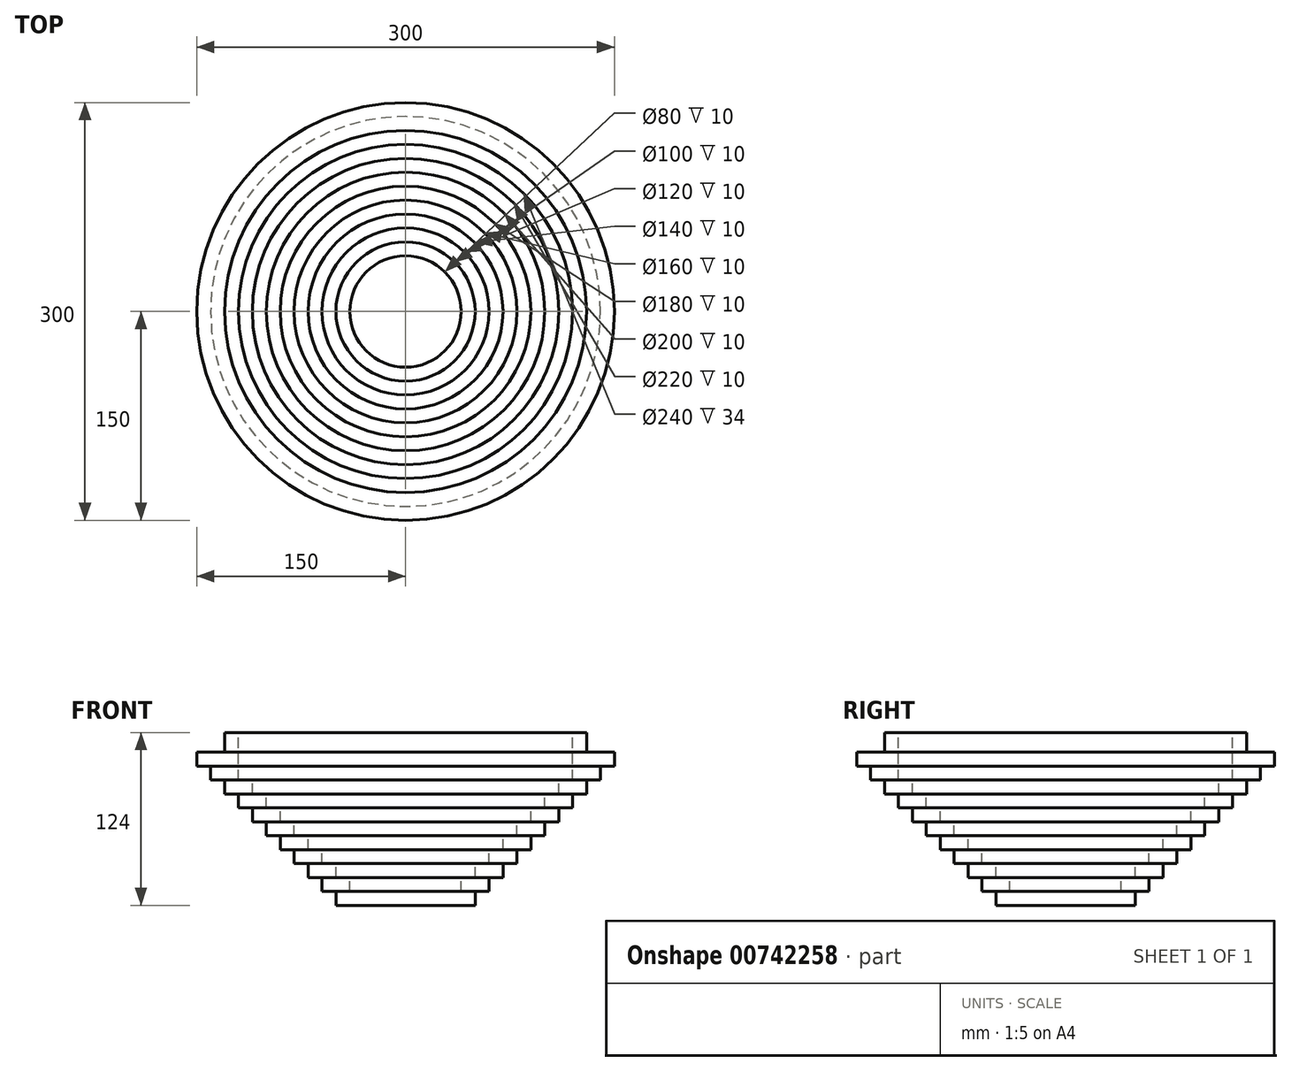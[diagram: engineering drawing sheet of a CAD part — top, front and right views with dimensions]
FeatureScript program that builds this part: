
annotation { "Feature Type Name" : "Feature", "Feature Type Description" : "" }
export const myFeature = defineFeature(function(context is Context, id is Id, definition is map)
    precondition{}
    {
        {
            var Q0;
            Q0=qCreatedBy(makeId("Front.planeOp"),FACE);
            var sketch = newSketch(context, id + "F0", { "sketchPlane" : qUnion([Q0])});
            skLineSegment(sketch, "E0", {"start": v(0, 0) * mm, "end": v(50, 0) * mm});
            skLineSegment(sketch, "E1", {"start": v(50, 0) * mm, "end": v(50, 10) * mm});
            skLineSegment(sketch, "E2", {"start": v(50, 10) * mm, "end": v(60, 10) * mm});
            skLineSegment(sketch, "E3", {"start": v(60, 10) * mm, "end": v(60, 20) * mm});
            skLineSegment(sketch, "E4", {"start": v(60, 20) * mm, "end": v(70, 20) * mm});
            skLineSegment(sketch, "E5", {"start": v(70, 20) * mm, "end": v(70, 30) * mm});
            skLineSegment(sketch, "E6", {"start": v(70, 30) * mm, "end": v(80, 30) * mm});
            skLineSegment(sketch, "E7", {"start": v(80, 30) * mm, "end": v(80, 40) * mm});
            skLineSegment(sketch, "E8", {"start": v(80, 40) * mm, "end": v(90, 40) * mm});
            skLineSegment(sketch, "E9", {"start": v(90, 40) * mm, "end": v(90, 50) * mm});
            skLineSegment(sketch, "E10", {"start": v(90, 50) * mm, "end": v(100, 50) * mm});
            skLineSegment(sketch, "E11", {"start": v(100, 50) * mm, "end": v(100, 60) * mm});
            skLineSegment(sketch, "E12", {"start": v(100, 60) * mm, "end": v(110, 60) * mm});
            skLineSegment(sketch, "E13", {"start": v(110, 60) * mm, "end": v(110, 70) * mm});
            skLineSegment(sketch, "E14", {"start": v(110, 70) * mm, "end": v(120, 70) * mm});
            skLineSegment(sketch, "E15", {"start": v(120, 70) * mm, "end": v(120, 80) * mm});
            skLineSegment(sketch, "E16", {"start": v(120, 80) * mm, "end": v(130, 80) * mm});
            skLineSegment(sketch, "E17", {"start": v(130, 80) * mm, "end": v(130, 90) * mm});
            skLineSegment(sketch, "E18", {"start": v(130, 90) * mm, "end": v(140, 90) * mm});
            skLineSegment(sketch, "E19", {"start": v(140, 90) * mm, "end": v(140, 100) * mm});
            skLineSegment(sketch, "E20", {"start": v(140, 100) * mm, "end": v(150, 100) * mm});
            skLineSegment(sketch, "E21", {"start": v(150, 100) * mm, "end": v(150, 110) * mm});
            skLineSegment(sketch, "E22.0", {"start": v(130, 100) * mm, "end": v(130, 110) * mm});
            skLineSegment(sketch, "E22.1", {"start": v(120, 100) * mm, "end": v(130, 100) * mm});
            skLineSegment(sketch, "E22.2", {"start": v(120, 90) * mm, "end": v(120, 100) * mm});
            skLineSegment(sketch, "E22.3", {"start": v(110, 90) * mm, "end": v(120, 90) * mm});
            skLineSegment(sketch, "E22.4", {"start": v(110, 80) * mm, "end": v(110, 90) * mm});
            skLineSegment(sketch, "E22.5", {"start": v(100, 80) * mm, "end": v(110, 80) * mm});
            skLineSegment(sketch, "E22.6", {"start": v(100, 70) * mm, "end": v(100, 80) * mm});
            skLineSegment(sketch, "E22.7", {"start": v(90, 70) * mm, "end": v(100, 70) * mm});
            skLineSegment(sketch, "E22.8", {"start": v(90, 60) * mm, "end": v(90, 70) * mm});
            skLineSegment(sketch, "E22.9", {"start": v(80, 60) * mm, "end": v(90, 60) * mm});
            skLineSegment(sketch, "E22.10", {"start": v(50, 20) * mm, "end": v(50, 30) * mm});
            skLineSegment(sketch, "E22.11", {"start": v(40, 20) * mm, "end": v(50, 20) * mm});
            skLineSegment(sketch, "E22.12", {"start": v(40, 10) * mm, "end": v(40, 20) * mm});
            skLineSegment(sketch, "E22.13", {"start": v(0, 10) * mm, "end": v(40, 10) * mm});
            skLineSegment(sketch, "E22.14", {"start": v(50, 30) * mm, "end": v(60, 30) * mm});
            skLineSegment(sketch, "E22.15", {"start": v(60, 30) * mm, "end": v(60, 40) * mm});
            skLineSegment(sketch, "E22.16", {"start": v(60, 40) * mm, "end": v(70, 40) * mm});
            skLineSegment(sketch, "E22.17", {"start": v(70, 40) * mm, "end": v(70, 50) * mm});
            skLineSegment(sketch, "E22.18", {"start": v(70, 50) * mm, "end": v(80, 50) * mm});
            skLineSegment(sketch, "E22.19", {"start": v(80, 50) * mm, "end": v(80, 60) * mm});
            skLineSegment(sketch, "E23", {"start": v(150, 110) * mm, "end": v(130, 110) * mm});
            skLineSegment(sketch, "E24", {"start": v(0, 10) * mm, "end": v(0, 0) * mm});
            skSolve(sketch);
        }
        {
            var Q0;
            Q0=makeQuery(id+"F0.imprint","IMPRINT",FACE,{"disambiguationData":[TD([[makeQuery(id+"F0.imprint","IMPRINT",EDGE,{"derivedFrom":sQuery(id+"F0.wireOp",EDGE,"E0")}),1.0]])]});
            var Q1;
            Q1=sQuery(id+"F0.wireOp",EDGE,"E24");
            revolve(context, id + "F1", {"surfaceOperationType" : NewSurfaceOperationType.NEW, "entities" : qUnion([Q0]), "axis" : qUnion([Q1]), "revolveType" : RevolveType.FULL});
        }
        {
            var Q0;
            Q0=makeQuery(id+"F1.opRevolve","SWEPT_FACE",FACE,{"disambiguationData":[OSD([sQuery(id+"F0.wireOp",EDGE,"E22.1")])]});
            var sketch = newSketch(context, id + "F2", { "sketchPlane" : qUnion([Q0])});
            skCircle(sketch, "E25", {"center": v(0, 0) * mm, "radius": 130 * mm});
            skCircle(sketch, "E26", {"center": v(0, 0) * mm, "radius": 120 * mm});
            skSolve(sketch);
        }
        {
            var Q0;
            Q0=makeQuery(id+"F2.imprint","IMPRINT",FACE,{"disambiguationData":[TD([[makeQuery(id+"F2.imprint","IMPRINT",EDGE,{"derivedFrom":sQuery(id+"F2.wireOp",EDGE,"E25")}),1.0]])]});
            extrude(context, id + "F3", {"entities" : qUnion([Q0]), "operationType" : NewBodyOperationType.ADD, "depth" : 24 * mm, "offsetDistance" : 25 * mm});
        }
    });
